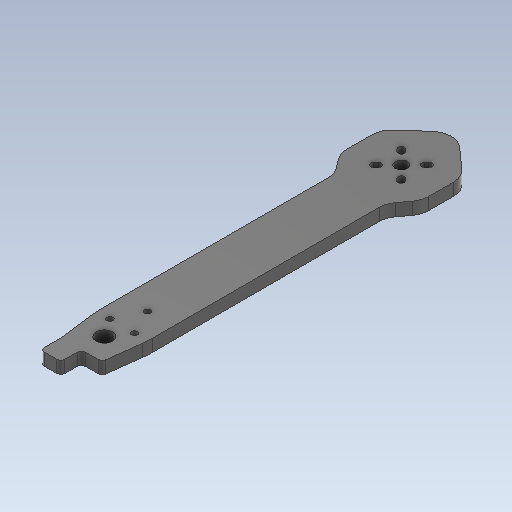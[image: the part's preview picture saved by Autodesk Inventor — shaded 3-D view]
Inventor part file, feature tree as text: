
AUTODESK INVENTOR PART (.ipt)
format: ipt  version: 2020 (Build 240168000, 168)  size: 193,024 bytes
history: native  units: in
note: dims shown in document units (in); Inventor stores cm internally (conversion verified against a paired STEP export)
features: sketch x1, projected_geometry x1
ambient origin geometry x8: Origin, YZ Plane, XZ Plane, XY Plane, X Axis, Y Axis, Z Axis, Center Point
bodies: Solid2 (feature_tree), Solid1 (feature_tree)
feature tree (2):
  sketch  "Sketch1"
  projected_geometry  "Projected Loop1"
